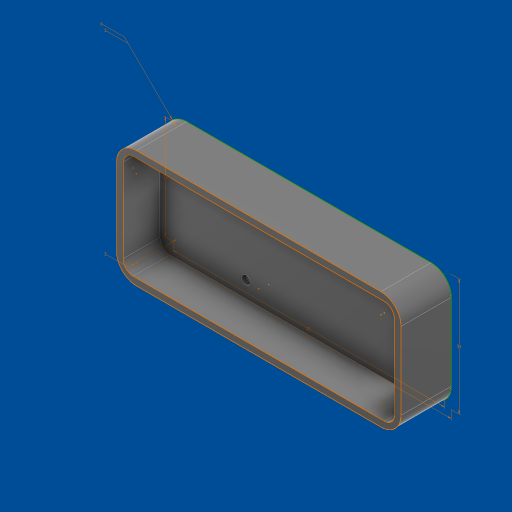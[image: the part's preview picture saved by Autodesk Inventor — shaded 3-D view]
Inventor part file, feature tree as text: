
AUTODESK INVENTOR PART (.ipt)
format: ipt  version: 2023.2 (Build 272271000, 271)  size: 260,096 bytes
history: native  units: mm
features: extrude x3, sketch x2, projected_geometry x1
ambient origin geometry x8: Origin, YZ Plane, XZ Plane, XY Plane, X Axis, Y Axis, Z Axis, Center Point
bodies: Solid1 (feature_tree)
feature tree (6):
  sketch  "Sketch1"  dims[d0=2.5mm d1=0.0mm d2=85.0mm]
  extrude  "Extrusion1"  Depth=85.0mm
  extrude  "Extrusion2"  Depth=6.0mm
  extrude  "Extrusion3"  Depth=81.0mm
  sketch  "Sketch3"  dims[d3=35.0mm d4=6.0mm d5=81.0mm d6=31.0mm d7=3.0mm d8=3.0mm d9=15.0mm d10=0.0mm d11=4.0mm d12=0.0mm]
  projected_geometry  "Projected Loop2"
